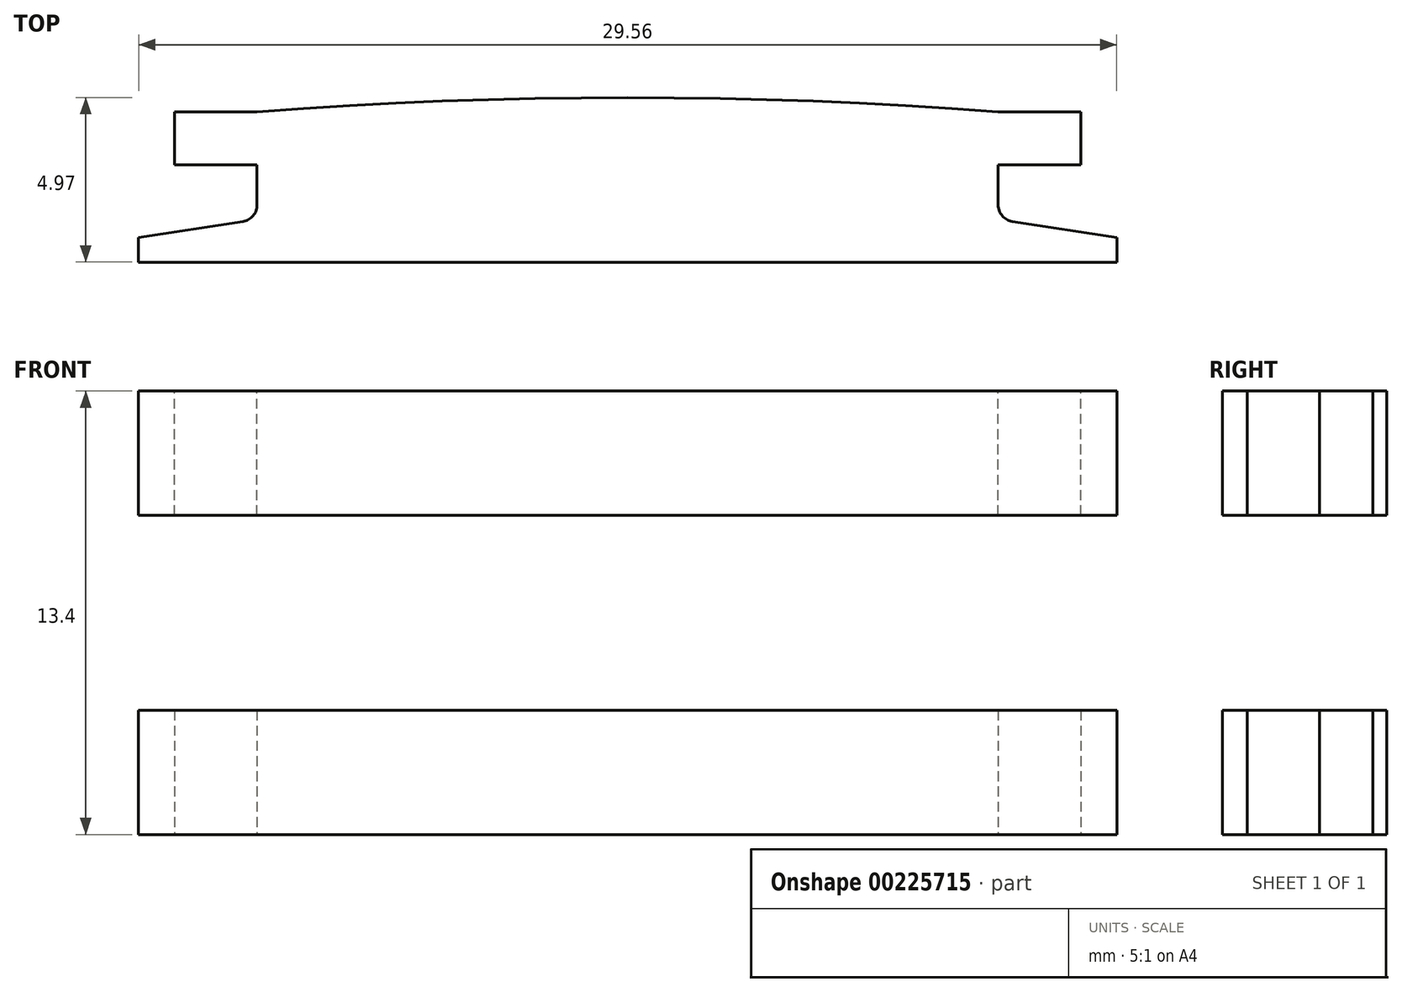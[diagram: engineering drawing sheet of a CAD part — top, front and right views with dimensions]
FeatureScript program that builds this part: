
annotation { "Feature Type Name" : "Feature", "Feature Type Description" : "" }
export const myFeature = defineFeature(function(context is Context, id is Id, definition is map)
    precondition{}
    {
        {
            var Q0;
            Q0=qCreatedBy(makeId("Top.planeOp"),FACE);
            var sketch = newSketch(context, id + "F0", { "sketchPlane" : qUnion([Q0])});
            skArc(sketch, "E0", {"start": v(11.2, 147.07) * mm, "mid": v(0, 147.5) * mm, "end": v(-11.2, 147.07) * mm});
            skLineSegment(sketch, "E1", {"start": v(0, 0) * mm, "end": v(11.2, 0) * mm, "construction": true});
            skLineSegment(sketch, "E2", {"start": v(11.2, 144.26) * mm, "end": v(11.2, 147.07) * mm});
            skLineSegment(sketch, "E3", {"start": v(0, 0) * mm, "end": v(0, 53.47) * mm, "construction": true});
            skLineSegment(sketch, "E4.MirrorCS", {"start": v(-11.2, 144.26) * mm, "end": v(-11.2, 147.07) * mm});
            skLineSegment(sketch, "E5", {"start": v(-11.2, 142.53) * mm, "end": v(11.2, 142.53) * mm});
            skPoint(sketch, "E6.orphan", {"position": v(-11.2, 0) * mm});
            skLineSegment(sketch, "E7", {"start": v(11.2, 142.53) * mm, "end": v(14.78, 142.53) * mm});
            skLineSegment(sketch, "E8", {"start": v(14.78, 142.53) * mm, "end": v(14.78, 143.28) * mm});
            skLineSegment(sketch, "E9", {"start": v(11.63, 143.76) * mm, "end": v(14.78, 143.28) * mm});
            skLineSegment(sketch, "E10.MirrorCS", {"start": v(-11.63, 143.76) * mm, "end": v(-14.78, 143.28) * mm});
            skLineSegment(sketch, "E11.MirrorCS", {"start": v(-11.2, 142.53) * mm, "end": v(-14.78, 142.53) * mm});
            skLineSegment(sketch, "E12.MirrorCS", {"start": v(-14.78, 142.53) * mm, "end": v(-14.78, 143.28) * mm});
            skPoint(sketch, "E13.visualSharp", {"position": v(11.2, 143.82) * mm});
            skArc(sketch, "E13.filletArc", {"start": v(11.2, 144.26) * mm, "mid": v(11.32, 143.93) * mm, "end": v(11.63, 143.76) * mm});
            skPoint(sketch, "E14.visualSharp", {"position": v(-11.2, 143.82) * mm});
            skArc(sketch, "E14.filletArc", {"start": v(-11.63, 143.76) * mm, "mid": v(-11.32, 143.93) * mm, "end": v(-11.2, 144.26) * mm});
            skSolve(sketch);
        }
        {
            var Q0;
            Q0=qSketchRegion(id+"F0",true);
            extrude(context, id + "F1", {"entities" : qUnion([Q0]), "depth" : 3.75 * mm});
        }
        {
            var Q0;
            Q0=makeQuery(id+"F1.opExtrude","CAP_FACE",FACE,{"disambiguationData":[OSD([sQuery(id+"F0.wireOp",EDGE,"E0"),sQuery(id+"F0.wireOp",EDGE,"E2"),sQuery(id+"F0.wireOp",EDGE,"E4.MirrorCS"),sQuery(id+"F0.wireOp",EDGE,"E5")])],"isStart":false});
            cPlane(context, id + "F2", {"entities" : qUnion([Q0]), "cplaneType" : CPlaneType.OFFSET, "offset" : 2.95 * mm, "width" : 150 * mm, "height" : 150 * mm});
        }
        {
            var Q0;
            Q0=makeQuery(id+"F1.opExtrude","SWEPT_FACE",FACE,{"disambiguationData":[OSD([sQuery(id+"F0.wireOp",EDGE,"E4.MirrorCS")])]});
            var sketch = newSketch(context, id + "F3", { "sketchPlane" : qUnion([Q0])});
            skLineSegment(sketch, "E15.bottom", {"start": v(-145.46, 3.75) * mm, "end": v(-147.07, 3.75) * mm});
            skLineSegment(sketch, "E15.top", {"start": v(-145.46, 0) * mm, "end": v(-147.07, 0) * mm});
            skLineSegment(sketch, "E15.left", {"start": v(-147.07, 3.75) * mm, "end": v(-147.07, 0) * mm});
            skLineSegment(sketch, "E15.right", {"start": v(-145.46, 3.75) * mm, "end": v(-145.46, 0) * mm});
            skSolve(sketch);
        }
        {
            var Q0;
            Q0=makeQuery(id+"F3.imprint","IMPRINT",FACE,{"disambiguationData":[TD([[makeQuery(id+"F3.imprint","IMPRINT",EDGE,{"derivedFrom":sQuery(id+"F3.wireOp",EDGE,"E15.bottom")}),1.0]])]});
            extrude(context, id + "F4", {"entities" : qUnion([Q0]), "operationType" : NewBodyOperationType.ADD, "depth" : 2.5 * mm});
        }
        {
            var Q0;
            Q0=makeQuery(id+"F1.opExtrude","SWEPT_BODY",BODY,{"disambiguationData":[OSD([sQuery(id+"F0.wireOp",EDGE,"E0"),sQuery(id+"F0.wireOp",EDGE,"E2"),sQuery(id+"F0.wireOp",EDGE,"E4.MirrorCS"),sQuery(id+"F0.wireOp",EDGE,"E5")])]});
            var Q1;
            Q1=qCreatedBy(makeId("Right.planeOp"),FACE);
            mirror(context, id + "F5", {"operationType" : NewBodyOperationType.ADD, "entities" : qUnion([Q0]), "mirrorPlane" : qUnion([Q1])});
        }
        {
            var Q0;
            Q0=makeQuery(id+"F1.opExtrude","SWEPT_BODY",BODY,{"disambiguationData":[OSD([sQuery(id+"F0.wireOp",EDGE,"E0"),sQuery(id+"F0.wireOp",EDGE,"E2"),sQuery(id+"F0.wireOp",EDGE,"E4.MirrorCS"),sQuery(id+"F0.wireOp",EDGE,"E5")])]});
            var Q1;
            Q1=qCreatedBy(id+"F2.planeOp",FACE);
            mirror(context, id + "F6", {"operationType" : NewBodyOperationType.ADD, "entities" : qUnion([Q0]), "mirrorPlane" : qUnion([Q1])});
        }
    });
